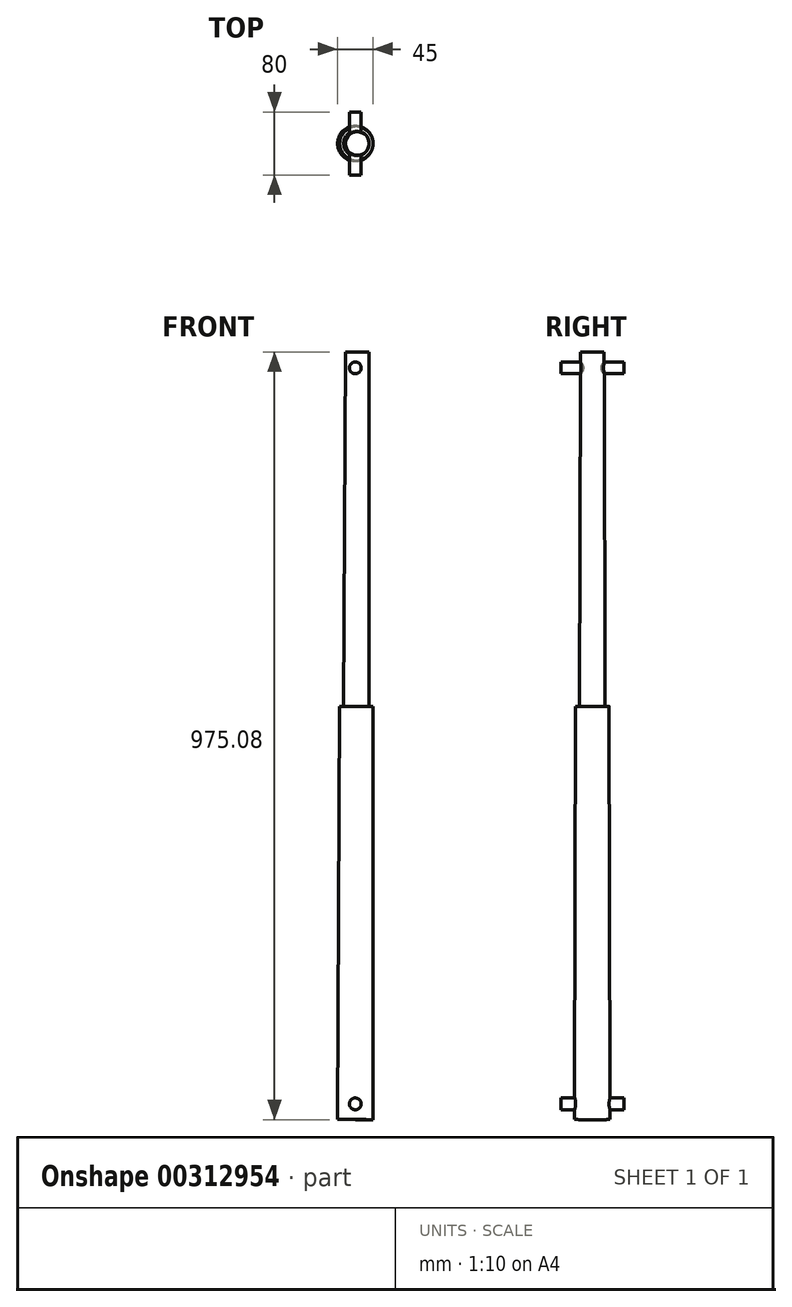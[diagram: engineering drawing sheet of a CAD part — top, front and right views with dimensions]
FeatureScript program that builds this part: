
annotation { "Feature Type Name" : "Feature", "Feature Type Description" : "" }
export const myFeature = defineFeature(function(context is Context, id is Id, definition is map)
    precondition{}
    {
        {
            var Q0;
            Q0=qCreatedBy(makeId("Front.planeOp"),FACE);
            var sketch = newSketch(context, id + "F0", { "sketchPlane" : qUnion([Q0])});
            skLineSegment(sketch, "E0", {"start": v(0, 0) * mm, "end": v(22.5, 0) * mm});
            skLineSegment(sketch, "E1", {"start": v(22.5, 0) * mm, "end": v(22.5, 525) * mm});
            skLineSegment(sketch, "E2", {"start": v(22.5, 525) * mm, "end": v(17.5, 525) * mm});
            skLineSegment(sketch, "E3", {"start": v(17.5, 525) * mm, "end": v(17.5, 975) * mm});
            skLineSegment(sketch, "E4", {"start": v(17.5, 975) * mm, "end": v(2.5, 975) * mm});
            skLineSegment(sketch, "E5", {"start": v(2.5, 975) * mm, "end": v(0, 0) * mm});
            skSolve(sketch);
        }
        {
            var Q0;
            Q0=makeQuery(id+"F0.imprint","IMPRINT",FACE,{"disambiguationData":[TD([[makeQuery(id+"F0.imprint","IMPRINT",EDGE,{"derivedFrom":sQuery(id+"F0.wireOp",EDGE,"E0")}),1.0]])]});
            var Q1;
            Q1=sQuery(id+"F0.wireOp",EDGE,"E5");
            revolve(context, id + "F1", {"entities" : qUnion([Q0]), "axis" : qUnion([Q1]), "revolveType" : RevolveType.FULL});
        }
        {
            var Q0;
            Q0=qCreatedBy(makeId("Front.planeOp"),FACE);
            var sketch = newSketch(context, id + "F2", { "sketchPlane" : qUnion([Q0])});
            skCircle(sketch, "E6", {"center": v(0, 20) * mm, "radius": 7.5 * mm});
            skCircle(sketch, "E7", {"center": v(0, 955) * mm, "radius": 7.5 * mm});
            skSolve(sketch);
        }
        {
            var Q0;
            Q0 = qSketchRegion(id + "F2", true);
            extrude(context, id + "F3", {"entities" : qUnion([Q0]), "operationType" : NewBodyOperationType.ADD, "endBound" : BoundingType.SYMMETRIC, "depth" : 80 * mm});
        }
    });
